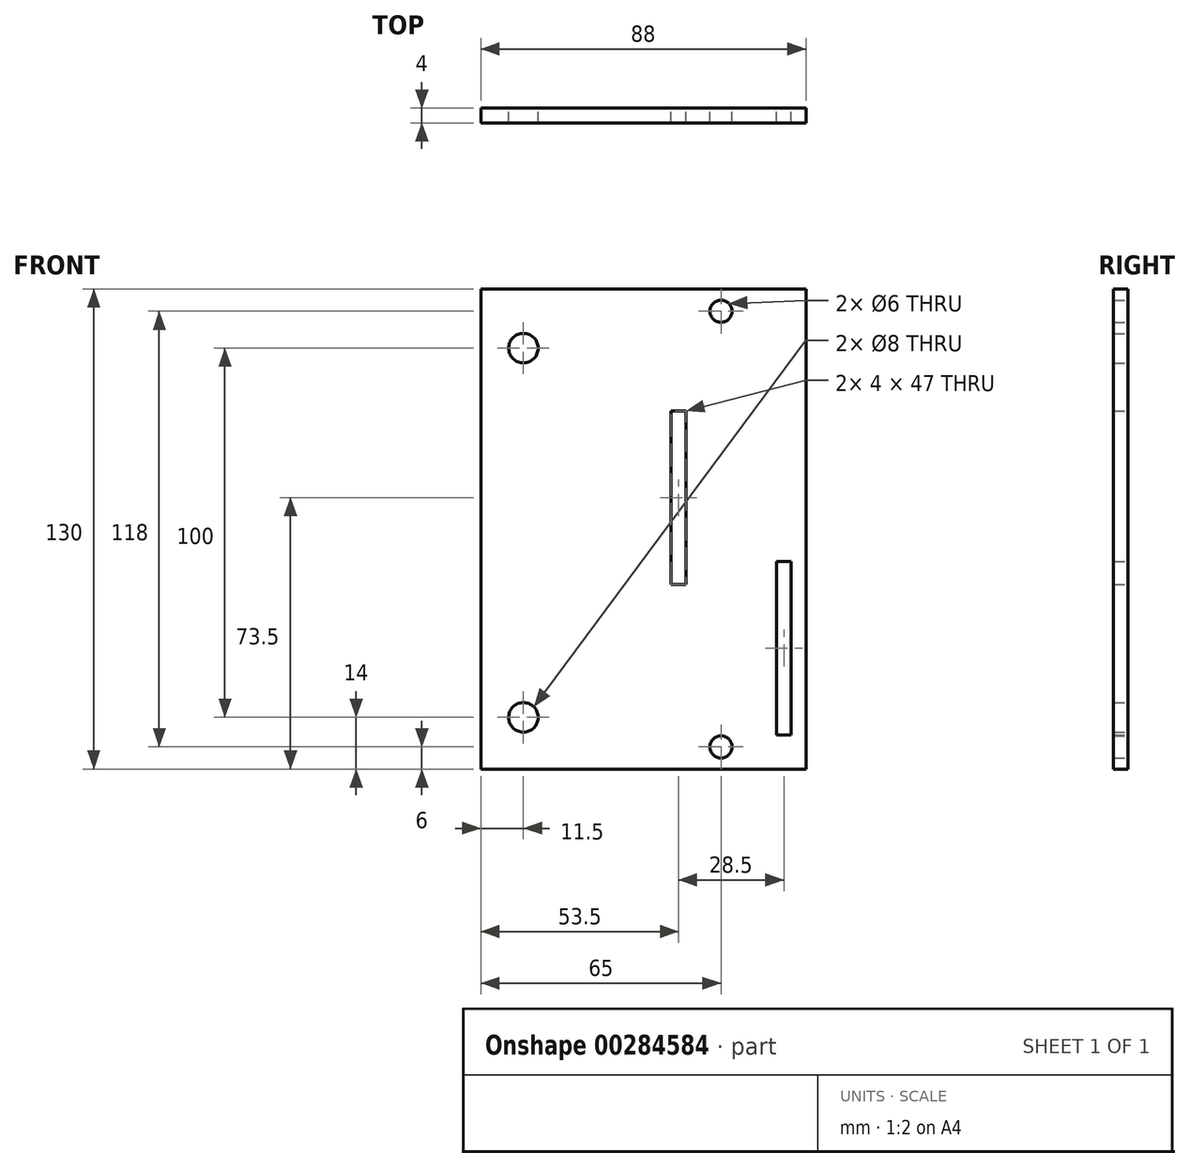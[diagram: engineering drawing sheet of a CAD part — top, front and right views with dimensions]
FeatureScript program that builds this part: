
annotation { "Feature Type Name" : "Feature", "Feature Type Description" : "" }
export const myFeature = defineFeature(function(context is Context, id is Id, definition is map)
    precondition{}
    {
        {
            var Q0;
            Q0=qCreatedBy(makeId("Front.planeOp"),FACE);
            var sketch = newSketch(context, id + "F0", { "sketchPlane" : qUnion([Q0])});
            skLineSegment(sketch, "E0.bottom", {"start": v(0, 0) * mm, "end": v(88, 0) * mm});
            skLineSegment(sketch, "E0.top", {"start": v(0, 130) * mm, "end": v(88, 130) * mm});
            skLineSegment(sketch, "E0.left", {"start": v(0, 0) * mm, "end": v(0, 130) * mm});
            skCircle(sketch, "E1", {"center": v(11.5, 114) * mm, "radius": 4 * mm});
            skCircle(sketch, "E2", {"center": v(11.5, 14) * mm, "radius": 4 * mm});
            skCircle(sketch, "E3", {"center": v(65, 124) * mm, "radius": 3 * mm});
            skCircle(sketch, "E4", {"center": v(65, 6) * mm, "radius": 3 * mm});
            skLineSegment(sketch, "E5.bottom", {"start": v(51.5, 97) * mm, "end": v(55.5, 97) * mm});
            skLineSegment(sketch, "E5.top", {"start": v(51.5, 50) * mm, "end": v(55.5, 50) * mm});
            skLineSegment(sketch, "E5.left", {"start": v(51.5, 97) * mm, "end": v(51.5, 50) * mm});
            skLineSegment(sketch, "E5.right", {"start": v(55.5, 97) * mm, "end": v(55.5, 50) * mm});
            skLineSegment(sketch, "E6.bottom", {"start": v(80, 56.25) * mm, "end": v(84, 56.25) * mm});
            skLineSegment(sketch, "E6.top", {"start": v(80, 9.25) * mm, "end": v(84, 9.25) * mm});
            skLineSegment(sketch, "E6.left", {"start": v(80, 56.25) * mm, "end": v(80, 9.25) * mm});
            skLineSegment(sketch, "E6.right", {"start": v(84, 56.25) * mm, "end": v(84, 9.25) * mm});
            skLineSegment(sketch, "E7", {"start": v(80, 32.75) * mm, "end": v(0, 32.75) * mm, "construction": true});
            skLineSegment(sketch, "E8.left", {"start": v(88, 130) * mm, "end": v(88, 0) * mm});
            skSolve(sketch);
        }
        {
            var Q0;
            Q0=qSketchRegion(id+"F0",true);
            extrude(context, id + "F1", {"entities" : qUnion([Q0]), "depth" : 4 * mm});
        }
    });
